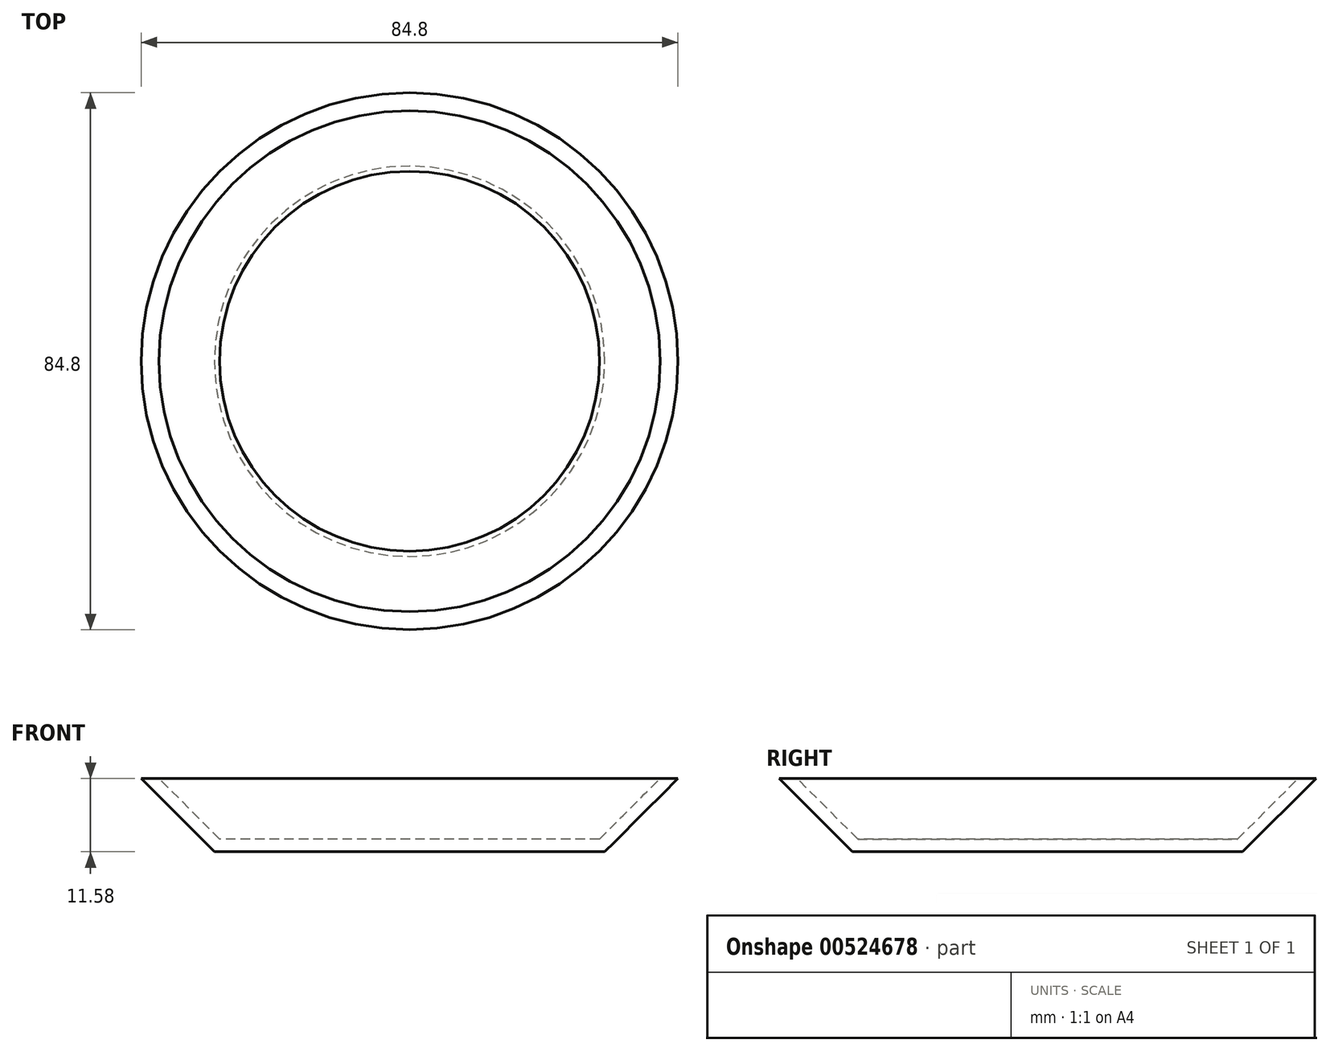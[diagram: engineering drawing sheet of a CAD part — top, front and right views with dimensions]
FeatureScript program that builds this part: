
annotation { "Feature Type Name" : "Feature", "Feature Type Description" : "" }
export const myFeature = defineFeature(function(context is Context, id is Id, definition is map)
    precondition{}
    {
        {
            var Q0;
            Q0=qCreatedBy(makeId("Front.planeOp"),FACE);
            var sketch = newSketch(context, id + "F0", { "sketchPlane" : qUnion([Q0])});
            skLineSegment(sketch, "E0.0", {"start": v(30, 2.1) * mm, "end": v(39.58, 11.67) * mm});
            skLineSegment(sketch, "E0.1", {"start": v(0, 2.1) * mm, "end": v(30, 2.1) * mm});
            skLineSegment(sketch, "E1.0", {"start": v(30.83, 0.1) * mm, "end": v(42.4, 11.67) * mm});
            skLineSegment(sketch, "E1.1", {"start": v(0, 0.1) * mm, "end": v(30.83, 0.1) * mm});
            skLineSegment(sketch, "E2", {"start": v(42.4, 11.67) * mm, "end": v(39.58, 11.67) * mm});
            skLineSegment(sketch, "E3", {"start": v(0, 2.1) * mm, "end": v(0, 0.1) * mm});
            skSolve(sketch);
        }
        {
            var Q0;
            Q0 = qSketchRegion(id + "F0", true);
            var Q1;
            Q1=sQuery(id+"F0.wireOp",EDGE,"E3");
            revolve(context, id + "F1", {"entities" : qUnion([Q0]), "axis" : qUnion([Q1]), "revolveType" : RevolveType.FULL});
        }
    });
